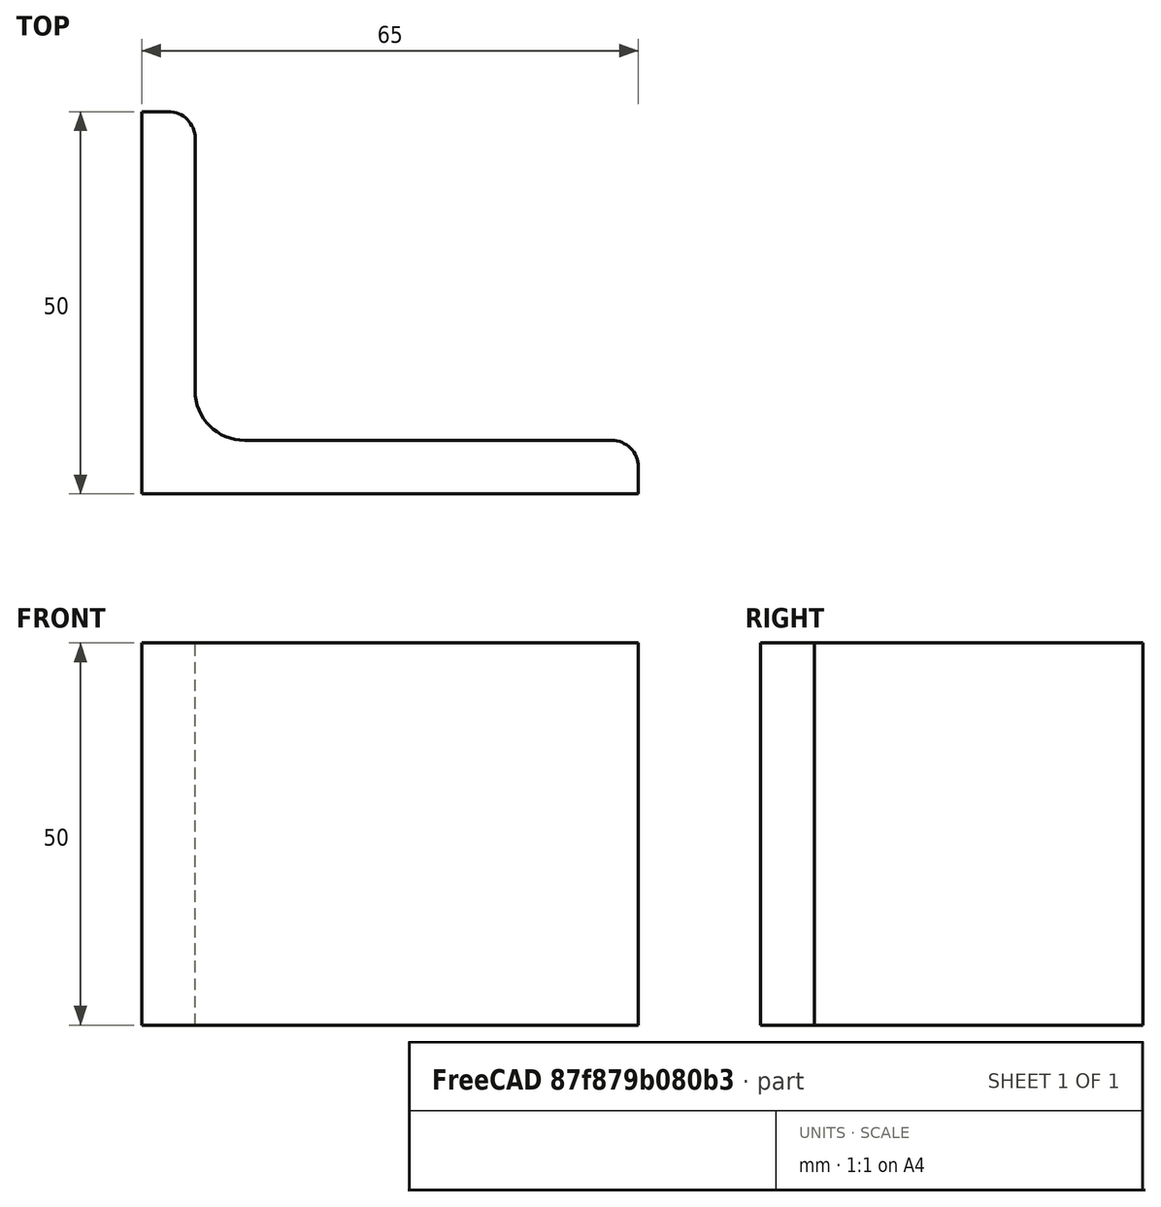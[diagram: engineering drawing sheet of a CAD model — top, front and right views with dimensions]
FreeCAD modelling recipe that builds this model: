
FCSTD DOCUMENT  (FreeCAD 0.15R4671 (Git))
Label: Angle Bar 65x50x7 EN10056 S235JR
License: All rights reserved
LicenseURL: http://en.wikipedia.org/wiki/All_rights_reserved
objects: Sketcher::SketchObject×1, Part::Extrusion×1
note: 2 computed .brp shape members not serialized (recipe doc carries the construction recipe); baked Part::Feature solids carry a one-line shape summary decoded from their .brp

FEATURE [Sketcher::SketchObject] Sketch
  sketch-geometry (9):
    g0: LineSegment StartX=0 StartY=0 StartZ=0 EndX=65 EndY=0 EndZ=0
    g1: LineSegment StartX=65 StartY=0 StartZ=0 EndX=65 EndY=3.5 EndZ=0
    g2: LineSegment StartX=61.5 StartY=7 StartZ=0 EndX=13.5 EndY=7 EndZ=0
    g3: LineSegment StartX=0 StartY=0 StartZ=0 EndX=0 EndY=50 EndZ=0
    g4: LineSegment StartX=0 StartY=50 StartZ=0 EndX=3.5 EndY=50 EndZ=0
    g5: LineSegment StartX=7 StartY=46.5 StartZ=0 EndX=7 EndY=13.5 EndZ=0
    g6: ArcOfCircle CenterX=13.5 CenterY=13.5 CenterZ=0 NormalX=0 NormalY=0 NormalZ=1 Radius=6.5 StartAngle=3.14159 EndAngle=4.71239
    g7: ArcOfCircle CenterX=3.5 CenterY=46.5 CenterZ=0 NormalX=0 NormalY=0 NormalZ=1 Radius=3.5 StartAngle=0 EndAngle=1.5708
    g8: ArcOfCircle CenterX=61.5 CenterY=3.5 CenterZ=0 NormalX=0 NormalY=0 NormalZ=1 Radius=3.5 StartAngle=0 EndAngle=1.5708
  constraints (23):
    c: Coincident(g0,g-1)
    c: Horizontal(g0)
    c: Coincident(g1,g0)
    c: Vertical(g1)
    c: Horizontal(g2)
    c: Coincident(g3,g-1)
    c: Vertical(g3)
    c: Coincident(g4,g3)
    c: Horizontal(g4)
    c: Vertical(g5)
    c: Tangent(g5,g6) = -1.5708
    c: Tangent(g2,g6) = 1.5708
    c: Tangent(g4,g7) = 1.5708
    c: Tangent(g5,g7) = 1.5708
    c: Tangent(g2,g8) = -1.5708
    c: Tangent(g1,g8) = -1.5708
    c: DistanceX(g0) = 65
    c: DistanceY(g3) = 50
    c: DistanceY(g0,g2) = 7
    c: DistanceX(g3,g5) = 7
    c: Radius(g6) = 6.5
    c: Radius(g8) = 3.5
    c: Radius(g7) = 3.5
FEATURE [Part::Extrusion] Extrude  label="Angle Bar 65x50x7 EN10056 S235JR"
  Base = -> Sketch
  Dir = (0,0,50)
  Solid = true
